# Revit family: Holyoake_-_CWD_Ceiling_Wash_Diffuser
name_source: partatom
category: Air Terminals
revit_build: Autodesk Revit 2014 (Build: 20130308_1515(x64)
units: mm (PartAtom-declared; Revit-internal decimal feet)

## types (5) — shared parameters
Array Parametric = 2
Bi Directional = No
D = 80 mm  [stored 0.262467 ft]
Default Elevation = 1219 mm
Flip Throw Direction = No
Flow = 0.0 L/s
Manufacturer = Holyoake
Material = <By Category>
Model = CWD
One Directional = Yes
Section = 2400 mm
Side 1 Closed = Yes
Side 1 Open = No
Side 2 Closed = No
Side 2 Open = No
Type Comments = Ceiling Wash Diffuser
URL = http://www.productspec.net
W = 89 mm  [stored 0.291995 ft]

## per-type parameters (varying)
| type | Array | Equal | L | Multiple | O | Remainder | Single |
| 600mm | 0.25 | No | 600 mm  [stored 1.9685 ft] | No | 634 mm  [stored 2.08005 ft] | 10 mm  [stored 0.0328084 ft] | Yes |
| 2400mm | 1 | No | 2400 mm | No | 2434 mm | 10 mm  [stored 0.0328084 ft] | Yes |
| 6000mm | 2.5 | No | 6000 mm  [stored 19.685 ft] | Yes | 6034 mm  [stored 19.7966 ft] | 600 mm  [stored 1.9685 ft] | No |
| 4800mm | 2 | Yes | 4800 mm | No | 4834 mm  [stored 15.8596 ft] | 10 mm  [stored 0.0328084 ft] | No |
| 1200mm | 0.5 | No | 1200 mm | No | 1234 mm | 10 mm  [stored 0.0328084 ft] | Yes |

note: [stored X ft] marks values corroborated as IEEE doubles in the binary element streams (Revit-internal decimal feet)

## geometry (parser evidence)
native form markers: Sweep x8
no freeform markers — native parametric forms only
